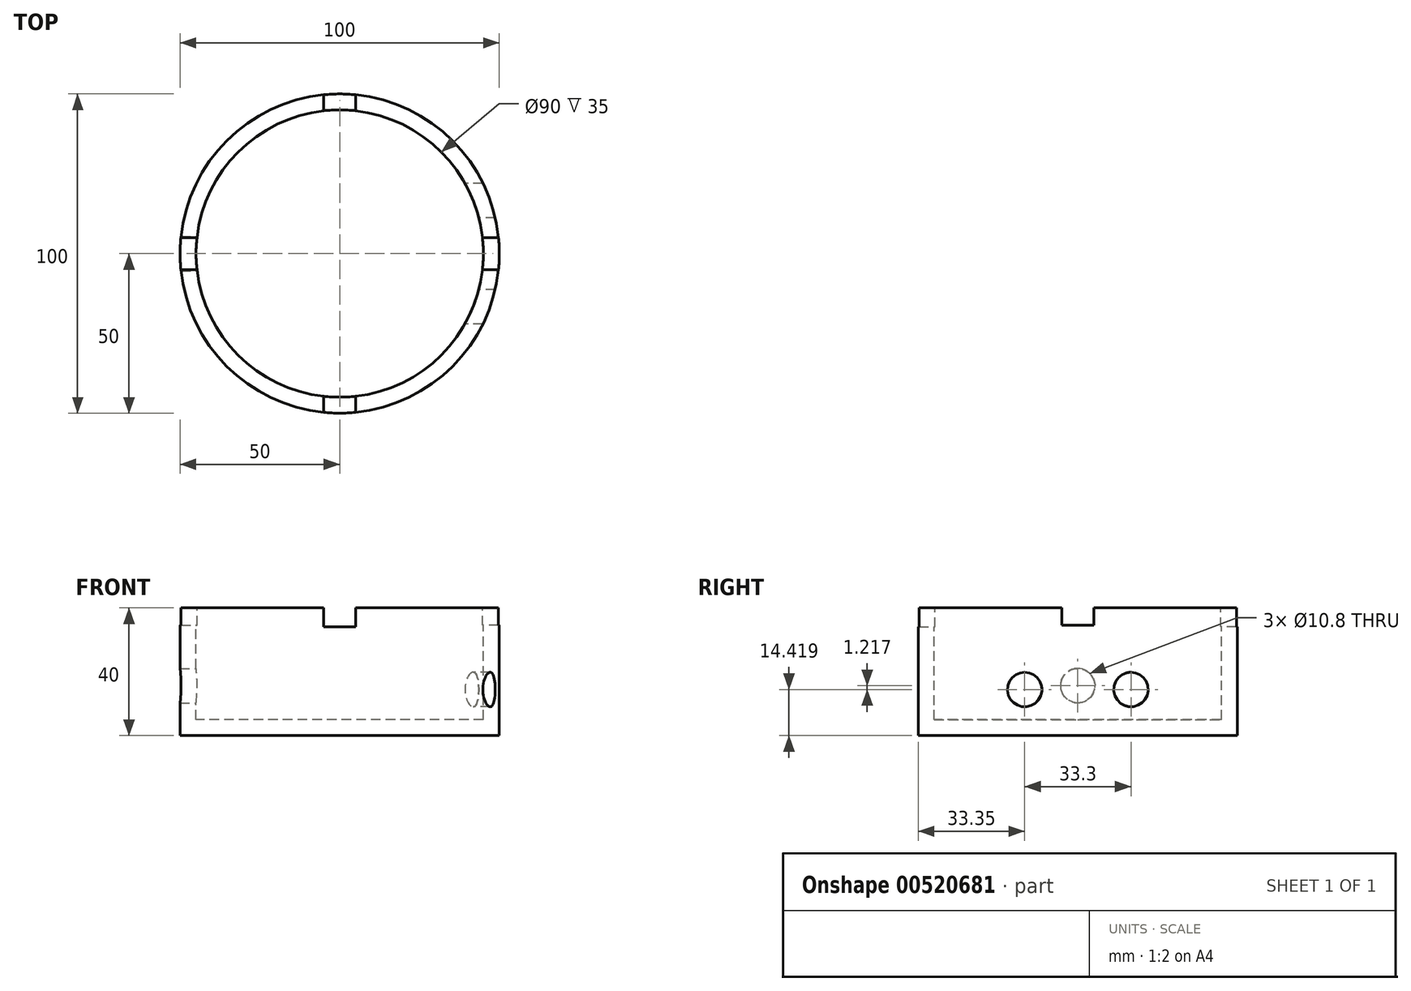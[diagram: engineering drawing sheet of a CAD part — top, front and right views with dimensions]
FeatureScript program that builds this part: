
annotation { "Feature Type Name" : "Feature", "Feature Type Description" : "" }
export const myFeature = defineFeature(function(context is Context, id is Id, definition is map)
    precondition{}
    {
        {
            var Q0;
            Q0=qCreatedBy(makeId("Top.planeOp"),FACE);
            var sketch = newSketch(context, id + "F0", { "sketchPlane" : qUnion([Q0])});
            skCircle(sketch, "E0", {"center": v(0, 0) * mm, "radius": 50 * mm});
            skSolve(sketch);
        }
        {
            var Q0;
            Q0=qSketchRegion(id+"F0",true);
            extrude(context, id + "F1", {"entities" : qUnion([Q0]), "depth" : 40 * mm, "offsetDistance" : 25 * mm});
        }
        {
            var Q0;
            Q0=makeQuery(id+"F1.opExtrude","CAP_FACE",FACE,{"disambiguationData":[OSD([sQuery(id+"F0.wireOp",EDGE,"E0")])],"isStart":false});
            var sketch = newSketch(context, id + "F2", { "sketchPlane" : qUnion([Q0])});
            skCircle(sketch, "E1", {"center": v(0, 0) * mm, "radius": 45 * mm});
            skSolve(sketch);
        }
        {
            var Q0;
            Q0=qSketchRegion(id+"F2",true);
            extrude(context, id + "F3", {"entities" : qUnion([Q0]), "operationType" : NewBodyOperationType.REMOVE, "oppositeDirection" : true, "depth" : 35 * mm, "offsetDistance" : 25 * mm});
        }
        {
            var Q0;
            Q0=qCreatedBy(makeId("Front.planeOp"),FACE);
            var sketch = newSketch(context, id + "F4", { "sketchPlane" : qUnion([Q0])});
            skLineSegment(sketch, "E2.bottom", {"start": v(5, 40) * mm, "end": v(-5, 40) * mm});
            skLineSegment(sketch, "E2.top", {"start": v(5, 34) * mm, "end": v(-5, 34) * mm});
            skLineSegment(sketch, "E2.left", {"start": v(5, 40) * mm, "end": v(5, 34) * mm});
            skLineSegment(sketch, "E2.right", {"start": v(-5, 40) * mm, "end": v(-5, 34) * mm});
            skSolve(sketch);
        }
        {
            var Q0;
            Q0=qSketchRegion(id+"F4",true);
            extrude(context, id + "F5", {"entities" : qUnion([Q0]), "operationType" : NewBodyOperationType.REMOVE, "oppositeDirection" : true, "depth" : 50 * mm, "offsetDistance" : 25 * mm});
        }
        {
            var Q0;
            Q0=qCreatedBy(makeId("Front.planeOp"),FACE);
            var sketch = newSketch(context, id + "F6", { "sketchPlane" : qUnion([Q0])});
            skLineSegment(sketch, "E3.bottom", {"start": v(5, 40) * mm, "end": v(-5, 40) * mm});
            skLineSegment(sketch, "E3.top", {"start": v(5, 34) * mm, "end": v(-5, 34) * mm});
            skLineSegment(sketch, "E3.left", {"start": v(5, 40) * mm, "end": v(5, 34) * mm});
            skLineSegment(sketch, "E3.right", {"start": v(-5, 40) * mm, "end": v(-5, 34) * mm});
            skSolve(sketch);
        }
        {
            var Q0;
            Q0=qSketchRegion(id+"F6",true);
            extrude(context, id + "F7", {"entities" : qUnion([Q0]), "operationType" : NewBodyOperationType.REMOVE, "depth" : 50 * mm, "offsetDistance" : 25 * mm});
        }
        {
            var Q0;
            Q0=qCreatedBy(makeId("Right.planeOp"),FACE);
            var sketch = newSketch(context, id + "F8", { "sketchPlane" : qUnion([Q0])});
            skLineSegment(sketch, "E4.bottom", {"start": v(5, 40) * mm, "end": v(-5, 40) * mm});
            skLineSegment(sketch, "E4.top", {"start": v(5, 34.5) * mm, "end": v(-5, 34.5) * mm});
            skLineSegment(sketch, "E4.left", {"start": v(5, 40) * mm, "end": v(5, 34.5) * mm});
            skLineSegment(sketch, "E4.right", {"start": v(-5, 40) * mm, "end": v(-5, 34.5) * mm});
            skSolve(sketch);
        }
        {
            var Q0;
            Q0=qSketchRegion(id+"F8",true);
            extrude(context, id + "F9", {"entities" : qUnion([Q0]), "operationType" : NewBodyOperationType.REMOVE, "oppositeDirection" : true, "depth" : 50 * mm, "offsetDistance" : 25 * mm});
        }
        {
            var Q0;
            Q0=qCreatedBy(makeId("Right.planeOp"),FACE);
            var sketch = newSketch(context, id + "F10", { "sketchPlane" : qUnion([Q0])});
            skLineSegment(sketch, "E5.bottom", {"start": v(5, 40) * mm, "end": v(-5, 40) * mm});
            skLineSegment(sketch, "E5.top", {"start": v(5, 34.5) * mm, "end": v(-5, 34.5) * mm});
            skLineSegment(sketch, "E5.left", {"start": v(5, 40) * mm, "end": v(5, 34.5) * mm});
            skLineSegment(sketch, "E5.right", {"start": v(-5, 40) * mm, "end": v(-5, 34.5) * mm});
            skSolve(sketch);
        }
        {
            var Q0;
            Q0=qSketchRegion(id+"F10",true);
            extrude(context, id + "F11", {"entities" : qUnion([Q0]), "operationType" : NewBodyOperationType.REMOVE, "depth" : 50 * mm, "offsetDistance" : 25 * mm});
        }
        {
            var Q0;
            Q0=qCreatedBy(makeId("Right.planeOp"),FACE);
            var sketch = newSketch(context, id + "F12", { "sketchPlane" : qUnion([Q0])});
            skCircle(sketch, "E6", {"center": v(-16.65, 14.42) * mm, "radius": 5.4 * mm});
            skCircle(sketch, "E7", {"center": v(16.65, 14.42) * mm, "radius": 5.4 * mm});
            skSolve(sketch);
        }
        {
            var Q0;
            Q0=qSketchRegion(id+"F12",true);
            extrude(context, id + "F13", {"entities" : qUnion([Q0]), "operationType" : NewBodyOperationType.REMOVE, "depth" : 59 * mm, "offsetDistance" : 25 * mm});
        }
        {
            var Q0;
            Q0=qCreatedBy(makeId("Right.planeOp"),FACE);
            var sketch = newSketch(context, id + "F14", { "sketchPlane" : qUnion([Q0])});
            skCircle(sketch, "E8", {"center": v(0, 15.64) * mm, "radius": 5.4 * mm});
            skSolve(sketch);
        }
        {
            var Q0;
            Q0=qSketchRegion(id+"F14",true);
            extrude(context, id + "F15", {"entities" : qUnion([Q0]), "operationType" : NewBodyOperationType.REMOVE, "oppositeDirection" : true, "depth" : 55 * mm, "offsetDistance" : 25 * mm});
        }
    });
